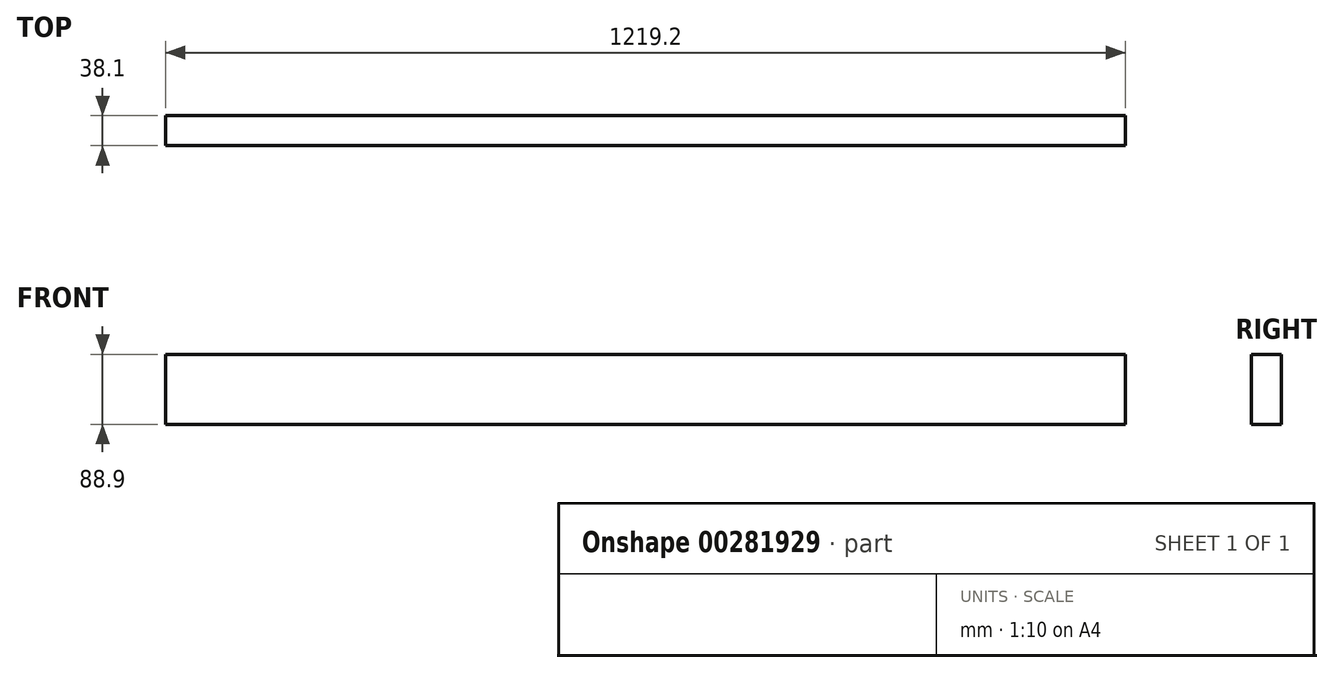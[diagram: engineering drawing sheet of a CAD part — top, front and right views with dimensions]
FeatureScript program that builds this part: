
annotation { "Feature Type Name" : "Feature", "Feature Type Description" : "" }
export const myFeature = defineFeature(function(context is Context, id is Id, definition is map)
    precondition{}
    {
        {
            var Q0;
            Q0=qCreatedBy(makeId("Right.planeOp"),FACE);
            var sketch = newSketch(context, id + "F0", { "sketchPlane" : qUnion([Q0])});
            skLineSegment(sketch, "E0.bottom", {"start": v(19.05, 44.45) * mm, "end": v(-19.05, 44.45) * mm});
            skLineSegment(sketch, "E0.top", {"start": v(19.05, -44.45) * mm, "end": v(-19.05, -44.45) * mm});
            skLineSegment(sketch, "E0.left", {"start": v(19.05, 44.45) * mm, "end": v(19.05, -44.45) * mm});
            skLineSegment(sketch, "E0.right", {"start": v(-19.05, 44.45) * mm, "end": v(-19.05, -44.45) * mm});
            skPoint(sketch, "E0.middle", {"position": v(0, 0) * mm});
            skSolve(sketch);
        }
        {
            var Q0;
            Q0=makeQuery(id+"F0.imprint","IMPRINT",FACE,{"disambiguationData":[TD([[makeQuery(id+"F0.imprint","IMPRINT",EDGE,{"derivedFrom":sQuery(id+"F0.wireOp",EDGE,"E0.bottom")}),1.0]])]});
            extrude(context, id + "F1", {"entities" : qUnion([Q0]), "depth" : 1219.2 * mm});
        }
    });
